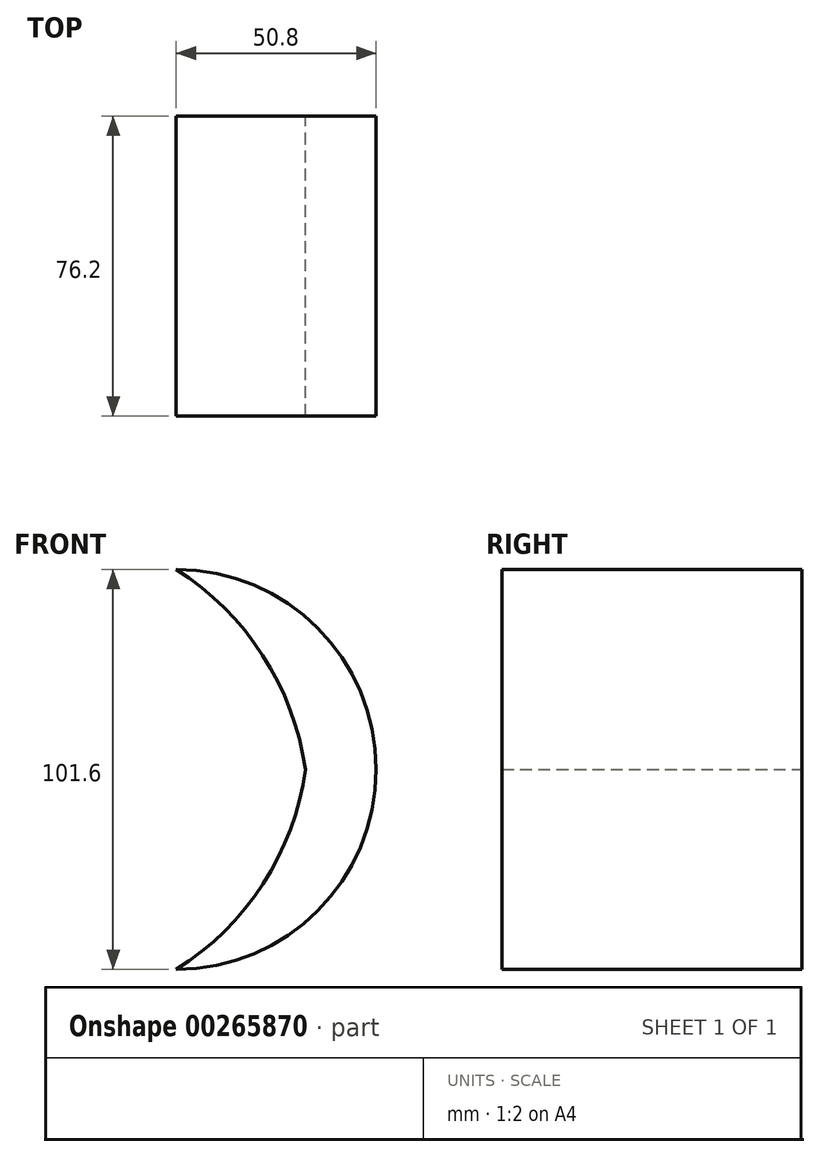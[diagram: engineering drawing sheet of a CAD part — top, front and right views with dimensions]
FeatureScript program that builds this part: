
annotation { "Feature Type Name" : "Feature", "Feature Type Description" : "" }
export const myFeature = defineFeature(function(context is Context, id is Id, definition is map)
    precondition{}
    {
        {
            var Q0;
            Q0=qCreatedBy(makeId("Front.planeOp"),FACE);
            var sketch = newSketch(context, id + "F0", { "sketchPlane" : qUnion([Q0])});
            skCircle(sketch, "E0", {"center": v(0, 0) * mm, "radius": 50.8 * mm});
            skArc(sketch, "E1", {"start": v(32.82, 0) * mm, "mid": v(21.98, 29) * mm, "end": v(0, 50.8) * mm});
            skArc(sketch, "E2", {"start": v(0, -50.8) * mm, "mid": v(22.1, -29.07) * mm, "end": v(32.82, 0) * mm});
            skSolve(sketch);
        }
        {
            var Q0;
            {var subQ0=sQuery(id+"F0.wireOp",EDGE,"E1");Q0=makeQuery(id+"F0.imprint","IMPRINT",FACE,{"disambiguationData":[TD([[makeQuery(id+"F0.imprint","IMPRINT",EDGE,{"derivedFrom":subQ0}),-1.0]])]});}
            extrude(context, id + "F1", {"entities" : qUnion([Q0]), "depth" : 76.2 * mm});
        }
    });
